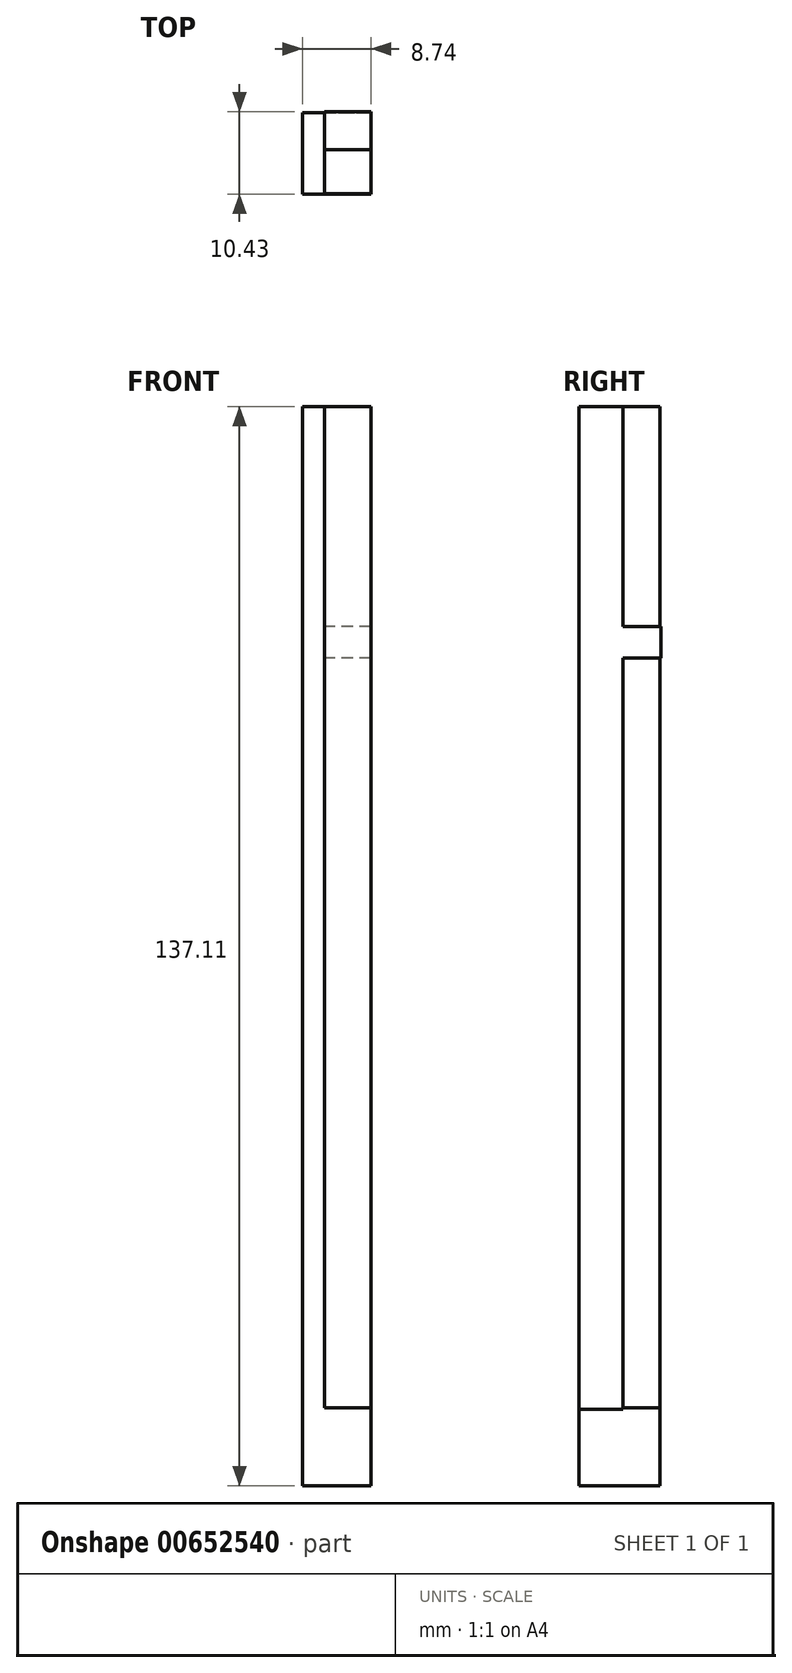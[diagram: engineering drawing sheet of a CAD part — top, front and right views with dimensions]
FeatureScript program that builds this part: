
annotation { "Feature Type Name" : "Feature", "Feature Type Description" : "" }
export const myFeature = defineFeature(function(context is Context, id is Id, definition is map)
    precondition{}
    {
        {
            var Q0;
            Q0=qCreatedBy(makeId("Front.planeOp"),FACE);
            var sketch = newSketch(context, id + "F0", { "sketchPlane" : qUnion([Q0])});
            skLineSegment(sketch, "E0.bottom", {"start": v(-4.7, 92.98) * mm, "end": v(5.6, 92.98) * mm});
            skLineSegment(sketch, "E0.top", {"start": v(-4.7, -34.22) * mm, "end": v(5.6, -34.22) * mm});
            skLineSegment(sketch, "E0.left", {"start": v(-4.7, 92.98) * mm, "end": v(-4.7, -34.22) * mm});
            skLineSegment(sketch, "E0.right", {"start": v(5.6, 92.98) * mm, "end": v(5.6, -34.22) * mm});
            skSolve(sketch);
        }
        {
            var Q0;
            Q0=makeQuery(id+"F0.imprint","IMPRINT",FACE,{"disambiguationData":[TD([[makeQuery(id+"F0.imprint","IMPRINT",EDGE,{"derivedFrom":sQuery(id+"F0.wireOp",EDGE,"E0.bottom")}),-1.0]])]});
            extrude(context, id + "F1", {"entities" : qUnion([Q0]), "oppositeDirection" : true, "depth" : 2.8 * mm, "offsetDistance" : 25.4 * mm});
        }
        {
            var Q0;
            Q0=qCreatedBy(makeId("Right.planeOp"),FACE);
            var sketch = newSketch(context, id + "F2", { "sketchPlane" : qUnion([Q0])});
            skLineSegment(sketch, "E1.bottom", {"start": v(0, 92.93) * mm, "end": v(8.74, 92.93) * mm});
            skLineSegment(sketch, "E1.top", {"start": v(0, -34.42) * mm, "end": v(8.74, -34.42) * mm});
            skLineSegment(sketch, "E1.left", {"start": v(0, 92.93) * mm, "end": v(0, -34.42) * mm});
            skLineSegment(sketch, "E1.right", {"start": v(8.74, 92.93) * mm, "end": v(8.74, -34.42) * mm});
            skSolve(sketch);
        }
        {
            var Q0;
            Q0=qSketchRegion(id+"F2",true);
            extrude(context, id + "F3", {"entities" : qUnion([Q0]), "operationType" : NewBodyOperationType.ADD, "depth" : 5.6 * mm, "offsetDistance" : 25.4 * mm});
        }
        {
            var Q0;
            Q0=makeQuery(id+"F1.opExtrude","SWEPT_FACE",FACE,{"disambiguationData":[OSD([sQuery(id+"F0.wireOp",EDGE,"E0.top")])]});
            var sketch = newSketch(context, id + "F4", { "sketchPlane" : qUnion([Q0])});
            skLineSegment(sketch, "E2.bottom", {"start": v(5.6, 0) * mm, "end": v(-4.7, 0) * mm});
            skLineSegment(sketch, "E2.top", {"start": v(5.6, -8.73) * mm, "end": v(-4.7, -8.73) * mm});
            skLineSegment(sketch, "E2.left", {"start": v(5.6, 0) * mm, "end": v(5.6, -8.73) * mm});
            skLineSegment(sketch, "E2.right", {"start": v(-4.7, 0) * mm, "end": v(-4.7, -8.73) * mm});
            skSolve(sketch);
        }
        {
            var Q0;
            Q0=qSketchRegion(id+"F4",true);
            extrude(context, id + "F5", {"entities" : qUnion([Q0]), "operationType" : NewBodyOperationType.ADD, "depth" : 9.9 * mm, "offsetDistance" : 25.4 * mm});
        }
        {
            var Q0;
            Q0=makeQuery(id+"F3.opExtrude","CAP_FACE",FACE,{"disambiguationData":[OSD([sQuery(id+"F2.wireOp",EDGE,"E1.bottom"),sQuery(id+"F2.wireOp",EDGE,"E1.top"),sQuery(id+"F2.wireOp",EDGE,"E1.left"),sQuery(id+"F2.wireOp",EDGE,"E1.right")])],"isStart":true});
            var sketch = newSketch(context, id + "F6", { "sketchPlane" : qUnion([Q0])});
            skLineSegment(sketch, "E3.bottom", {"start": v(-8.74, 65.01) * mm, "end": v(-2.8, 65.01) * mm});
            skLineSegment(sketch, "E3.top", {"start": v(-8.74, 61) * mm, "end": v(-2.8, 61) * mm});
            skLineSegment(sketch, "E3.left", {"start": v(-8.74, 65.01) * mm, "end": v(-8.74, 61) * mm});
            skLineSegment(sketch, "E3.right", {"start": v(-2.8, 65.01) * mm, "end": v(-2.8, 61) * mm});
            skSolve(sketch);
        }
        {
            var Q0;
            Q0=qSketchRegion(id+"F6",true);
            extrude(context, id + "F7", {"entities" : qUnion([Q0]), "operationType" : NewBodyOperationType.ADD, "depth" : 4.83 * mm, "offsetDistance" : 25.4 * mm});
        }
        {
            var Q0;
            Q0=makeQuery(id+"F1.opExtrude","SWEPT_BODY",BODY,{"disambiguationData":[OSD([sQuery(id+"F0.wireOp",EDGE,"E0.bottom"),sQuery(id+"F0.wireOp",EDGE,"E0.top"),sQuery(id+"F0.wireOp",EDGE,"E0.left"),sQuery(id+"F0.wireOp",EDGE,"E0.right")])]});
            var Q1;
            Q1=makeQuery(id+"F5.opExtrude","SWEPT_EDGE",EDGE,{"disambiguationData":[OSD([sQuery(id+"F4.wireOp",EDGE,"E2.bottom"),sQuery(id+"F4.wireOp",EDGE,"E2.right")])]});
            transform(context, id + "F8", {"entities" : qUnion([Q0]), "transformType" : TransformType.ROTATION, "transformAxis" : qUnion([Q1]), "angle" : 270 * degree, "makeCopy" : false});
        }
    });
